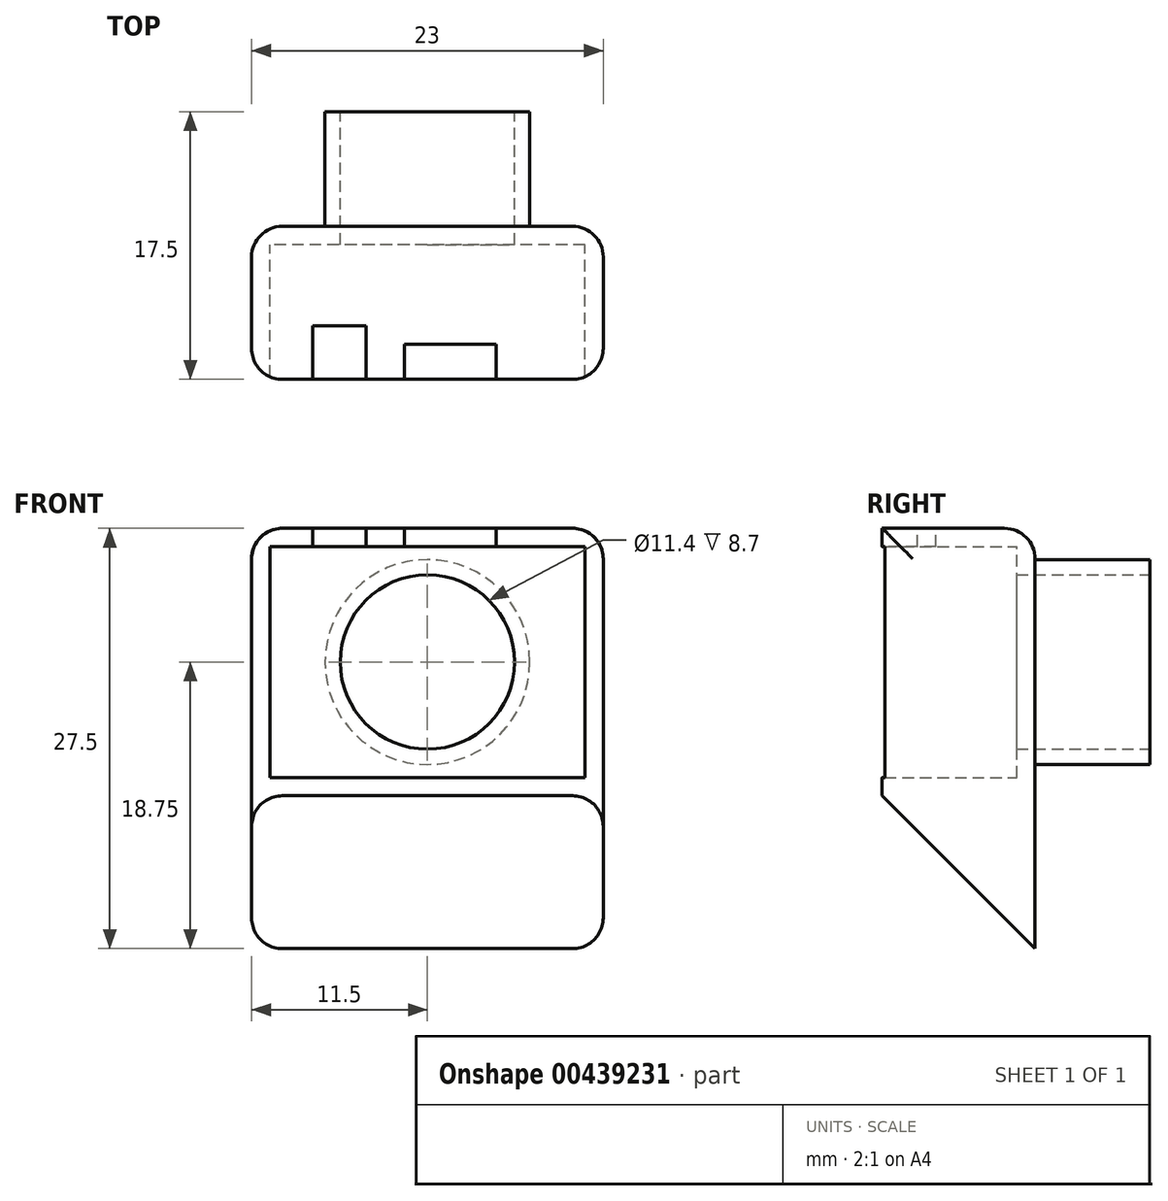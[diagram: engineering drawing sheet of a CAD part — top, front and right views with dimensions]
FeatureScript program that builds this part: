
annotation { "Feature Type Name" : "Feature", "Feature Type Description" : "" }
export const myFeature = defineFeature(function(context is Context, id is Id, definition is map)
    precondition{}
    {
        {
            var Q0;
            Q0=qCreatedBy(makeId("Front.planeOp"),FACE);
            var sketch = newSketch(context, id + "F0", { "sketchPlane" : qUnion([Q0])});
            skLineSegment(sketch, "E0.bottom", {"start": v(11.5, -8.75) * mm, "end": v(-11.5, -8.75) * mm});
            skLineSegment(sketch, "E0.top", {"start": v(11.5, 8.75) * mm, "end": v(-11.5, 8.75) * mm});
            skLineSegment(sketch, "E0.left", {"start": v(11.5, -8.75) * mm, "end": v(11.5, 8.75) * mm});
            skLineSegment(sketch, "E0.right", {"start": v(-11.5, -8.75) * mm, "end": v(-11.5, 8.75) * mm});
            skPoint(sketch, "E0.middle", {"position": v(0, 0) * mm});
            skSolve(sketch);
        }
        {
            var Q0;
            Q0 = qSketchRegion(id + "F0", true);
            extrude(context, id + "F1", {"entities" : qUnion([Q0]), "depth" : 10 * mm, "offsetDistance" : 25 * mm});
        }
        {
            var Q0;
            Q0=makeQuery(id+"F1.opExtrude","CAP_FACE",FACE,{"disambiguationData":[OSD([sQuery(id+"F0.wireOp",EDGE,"E0.bottom"),sQuery(id+"F0.wireOp",EDGE,"E0.top"),sQuery(id+"F0.wireOp",EDGE,"E0.left"),sQuery(id+"F0.wireOp",EDGE,"E0.right")])],"isStart":false});
            shell(context, id + "F2", {"entities" : qUnion([Q0]), "thickness" : 1.2 * mm});
        }
        {
            var Q0;
            Q0=makeQuery(id+"F1.opExtrude","CAP_FACE",FACE,{"disambiguationData":[OSD([sQuery(id+"F0.wireOp",EDGE,"E0.bottom"),sQuery(id+"F0.wireOp",EDGE,"E0.top"),sQuery(id+"F0.wireOp",EDGE,"E0.left"),sQuery(id+"F0.wireOp",EDGE,"E0.right")])],"isStart":true});
            var sketch = newSketch(context, id + "F3", { "sketchPlane" : qUnion([Q0])});
            skCircle(sketch, "E1", {"center": v(0, 0) * mm, "radius": 5.7 * mm});
            skCircle(sketch, "E2.0", {"center": v(0, 0) * mm, "radius": 6.7 * mm});
            skSolve(sketch);
        }
        {
            var Q0;
            Q0=makeQuery(id+"F3.imprint","IMPRINT",FACE,{"disambiguationData":[TD([[makeQuery(id+"F3.imprint","IMPRINT",EDGE,{"derivedFrom":sQuery(id+"F3.wireOp",EDGE,"E1")}),1.0]])]});
            extrude(context, id + "F4", {"entities" : qUnion([Q0]), "operationType" : NewBodyOperationType.REMOVE, "oppositeDirection" : true, "depth" : 3 * mm, "offsetDistance" : 25 * mm});
        }
        {
            var Q0;
            Q0=makeQuery(id+"F3.imprint","IMPRINT",FACE,{"disambiguationData":[TD([[makeQuery(id+"F3.imprint","IMPRINT",EDGE,{"derivedFrom":sQuery(id+"F3.wireOp",EDGE,"E1")}),-1.0]])]});
            extrude(context, id + "F5", {"entities" : qUnion([Q0]), "operationType" : NewBodyOperationType.ADD, "depth" : 7.5 * mm, "offsetDistance" : 25 * mm});
        }
        {
            var Q0;
            Q0=makeQuery(id+"F1.opExtrude","SWEPT_FACE",FACE,{"disambiguationData":[OSD([sQuery(id+"F0.wireOp",EDGE,"E0.top")])]});
            var sketch = newSketch(context, id + "F6", { "sketchPlane" : qUnion([Q0])});
            skLineSegment(sketch, "E3.bottom", {"start": v(4.5, -10) * mm, "end": v(-1.5, -10) * mm});
            skLineSegment(sketch, "E3.top", {"start": v(4.5, -7.7) * mm, "end": v(-1.5, -7.7) * mm});
            skLineSegment(sketch, "E3.left", {"start": v(4.5, -10) * mm, "end": v(4.5, -7.7) * mm});
            skLineSegment(sketch, "E3.right", {"start": v(-1.5, -10) * mm, "end": v(-1.5, -7.7) * mm});
            skLineSegment(sketch, "E4.bottom", {"start": v(-1.5, -7.7) * mm, "end": v(4.5, -7.7) * mm});
            skLineSegment(sketch, "E4.top", {"start": v(-1.5, -5.4) * mm, "end": v(4.5, -5.4) * mm});
            skLineSegment(sketch, "E4.left", {"start": v(-1.5, -7.7) * mm, "end": v(-1.5, -5.4) * mm});
            skLineSegment(sketch, "E4.right", {"start": v(4.5, -7.7) * mm, "end": v(4.5, -5.4) * mm});
            skLineSegment(sketch, "E5.bottom", {"start": v(-7.5, -10) * mm, "end": v(-4, -10) * mm});
            skLineSegment(sketch, "E5.top", {"start": v(-7.5, -6.5) * mm, "end": v(-4, -6.5) * mm});
            skLineSegment(sketch, "E5.left", {"start": v(-7.5, -10) * mm, "end": v(-7.5, -6.5) * mm});
            skLineSegment(sketch, "E5.right", {"start": v(-4, -10) * mm, "end": v(-4, -6.5) * mm});
            skSolve(sketch);
        }
        {
            var Q0;
            Q0=makeQuery(id+"F6.imprint","IMPRINT",FACE,{"disambiguationData":[TD([[makeQuery(id+"F6.imprint","IMPRINT",EDGE,{"derivedFrom":sQuery(id+"F6.wireOp",EDGE,"E3.bottom")}),-1.0]])]});
            var Q1;
            Q1=makeQuery(id+"F6.imprint","IMPRINT",FACE,{"disambiguationData":[TD([[makeQuery(id+"F6.imprint","IMPRINT",EDGE,{"derivedFrom":sQuery(id+"F6.wireOp",EDGE,"E5.bottom")}),-1.0]])]});
            extrude(context, id + "F7", {"entities" : qUnion([Q0, Q1]), "operationType" : NewBodyOperationType.REMOVE, "oppositeDirection" : true, "depth" : 4 * mm, "offsetDistance" : 25 * mm});
        }
        {
            var Q0;
            Q0=makeQuery(id+"F1.opExtrude","SWEPT_FACE",FACE,{"disambiguationData":[OSD([sQuery(id+"F0.wireOp",EDGE,"E0.bottom")])]});
            extrude(context, id + "F8", {"entities" : qUnion([Q0]), "operationType" : NewBodyOperationType.ADD, "depth" : 10 * mm, "offsetDistance" : 25 * mm});
        }
        {
            var Q0;
            {var subQ0=sQuery(id+"F0.wireOp",EDGE,"E0.left");Q0=makeQuery(id+"F8.boolean.opBoolean","MERGE",FACE,{"derivedFrom":[makeQuery(id+"F1.opExtrude","SWEPT_FACE",FACE,{"disambiguationData":[OSD([subQ0])]}),makeQuery(id+"F8.opExtrude","SWEPT_FACE",FACE,{"disambiguationData":[OSD([sQuery(id+"F0.wireOp",EDGE,"E0.bottom"),subQ0])]})]});}
            var sketch = newSketch(context, id + "F9", { "sketchPlane" : qUnion([Q0])});
            skLineSegment(sketch, "E6", {"start": v(0, -18.75) * mm, "end": v(-10, -8.75) * mm});
            skSolve(sketch);
        }
        {
            var Q0;
            {var subQ0=sQuery(id+"F9.wireOp",EDGE,"E6");Q0=makeQuery(id+"F9.imprint","IMPRINT",FACE,{"disambiguationData":[TD([[makeQuery(id+"F9.imprint","IMPRINT",EDGE,{"derivedFrom":subQ0}),1.0]])]});}
            extrude(context, id + "F10", {"entities" : qUnion([Q0]), "operationType" : NewBodyOperationType.REMOVE, "oppositeDirection" : true, "depth" : 30 * mm, "offsetDistance" : 25 * mm});
        }
        {
            var Q0;
            Q0=makeQuery(id+"F1.opExtrude","CAP_EDGE",EDGE,{"disambiguationData":[OSD([sQuery(id+"F0.wireOp",EDGE,"E0.top")])],"isStart":true});
            var Q1;
            {var subQ0=sQuery(id+"F0.wireOp",EDGE,"E0.right");var subQ1=sQuery(id+"F0.wireOp",EDGE,"E0.bottom");Q1=makeQuery(id+"F8.boolean.opBoolean","MERGE",EDGE,{"derivedFrom":[makeQuery(id+"F1.opExtrude","CAP_EDGE",EDGE,{"disambiguationData":[OSD([subQ0])],"isStart":true}),makeQuery(id+"F8.opExtrude","SWEPT_EDGE",EDGE,{"disambiguationData":[OSD([subQ1,subQ0]),TDD([makeQuery(id+"F1.opExtrude","CAP_VERTEX",VERTEX,{"disambiguationData":[OSD([subQ1,subQ0])],"isStart":true})])]})]});}
            var Q2;
            {var subQ0=sQuery(id+"F0.wireOp",EDGE,"E0.left");var subQ1=sQuery(id+"F0.wireOp",EDGE,"E0.bottom");Q2=makeQuery(id+"F8.boolean.opBoolean","MERGE",EDGE,{"derivedFrom":[makeQuery(id+"F1.opExtrude","CAP_EDGE",EDGE,{"disambiguationData":[OSD([subQ0])],"isStart":true}),makeQuery(id+"F8.opExtrude","SWEPT_EDGE",EDGE,{"disambiguationData":[OSD([subQ1,subQ0]),TDD([makeQuery(id+"F1.opExtrude","CAP_VERTEX",VERTEX,{"disambiguationData":[OSD([subQ1,subQ0])],"isStart":true})])]})]});}
            var Q3;
            Q3=makeQuery(id+"F1.opExtrude","SWEPT_EDGE",EDGE,{"disambiguationData":[OSD([sQuery(id+"F0.wireOp",EDGE,"E0.top"),sQuery(id+"F0.wireOp",EDGE,"E0.left")])]});
            var Q4;
            Q4=makeQuery(id+"F1.opExtrude","SWEPT_EDGE",EDGE,{"disambiguationData":[OSD([sQuery(id+"F0.wireOp",EDGE,"E0.top"),sQuery(id+"F0.wireOp",EDGE,"E0.right")])]});
            var Q5;
            {var subQ0=sQuery(id+"F0.wireOp",EDGE,"E0.left");var subQ1=sQuery(id+"F0.wireOp",EDGE,"E0.bottom");Q5=makeQuery(id+"F8.boolean.opBoolean","MERGE",EDGE,{"derivedFrom":[makeQuery(id+"F1.opExtrude","CAP_EDGE",EDGE,{"disambiguationData":[OSD([subQ0])],"isStart":false}),makeQuery(id+"F8.opExtrude","SWEPT_EDGE",EDGE,{"disambiguationData":[OSD([subQ1,subQ0]),TDD([makeQuery(id+"F1.opExtrude","CAP_VERTEX",VERTEX,{"disambiguationData":[OSD([subQ1,subQ0])],"isStart":false})])]})]});}
            var Q6;
            {var subQ0=sQuery(id+"F0.wireOp",EDGE,"E0.right");var subQ1=sQuery(id+"F0.wireOp",EDGE,"E0.bottom");Q6=makeQuery(id+"F8.boolean.opBoolean","MERGE",EDGE,{"derivedFrom":[makeQuery(id+"F1.opExtrude","CAP_EDGE",EDGE,{"disambiguationData":[OSD([subQ0])],"isStart":false}),makeQuery(id+"F8.opExtrude","SWEPT_EDGE",EDGE,{"disambiguationData":[OSD([subQ1,subQ0]),TDD([makeQuery(id+"F1.opExtrude","CAP_VERTEX",VERTEX,{"disambiguationData":[OSD([subQ1,subQ0])],"isStart":false})])]})]});}
            fillet(context, id + "F11", {"entities" : qUnion([Q0, Q1, Q2, Q3, Q4, Q5, Q6]), "radius" : 2 * mm, "tangentPropagation" : true, "allowEdgeOverflow" : false});
        }
    });
